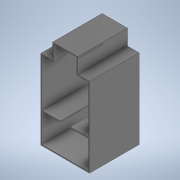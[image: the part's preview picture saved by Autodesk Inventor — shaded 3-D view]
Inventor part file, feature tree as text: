
AUTODESK INVENTOR PART (.ipt)
format: ipt  version: 2020 (Build 240168000, 168)  size: 200,704 bytes
history: native  units: mm
features: extrude x4, sketch x4, projected_geometry x2, other x1
ambient origin geometry x8: Origin, YZ Plane, XZ Plane, XY Plane, X Axis, Y Axis, Z Axis, Center Point
bodies: Body1 (feature_tree)
feature tree (11):
  other  "솔리드1"
  extrude  "돌출1"  Depth=500.0mm
  extrude  "돌출2"  Depth=820.0mm
  extrude  "돌출3"  Depth=820.0mm
  extrude  "돌출4"  Depth=10.0mm
  sketch  "스케치1"
  sketch  "스케치2"
  projected_geometry  "투영된 루프1"
  sketch  "스케치3"
  projected_geometry  "투영된 루프2"
  sketch  "스케치4"
